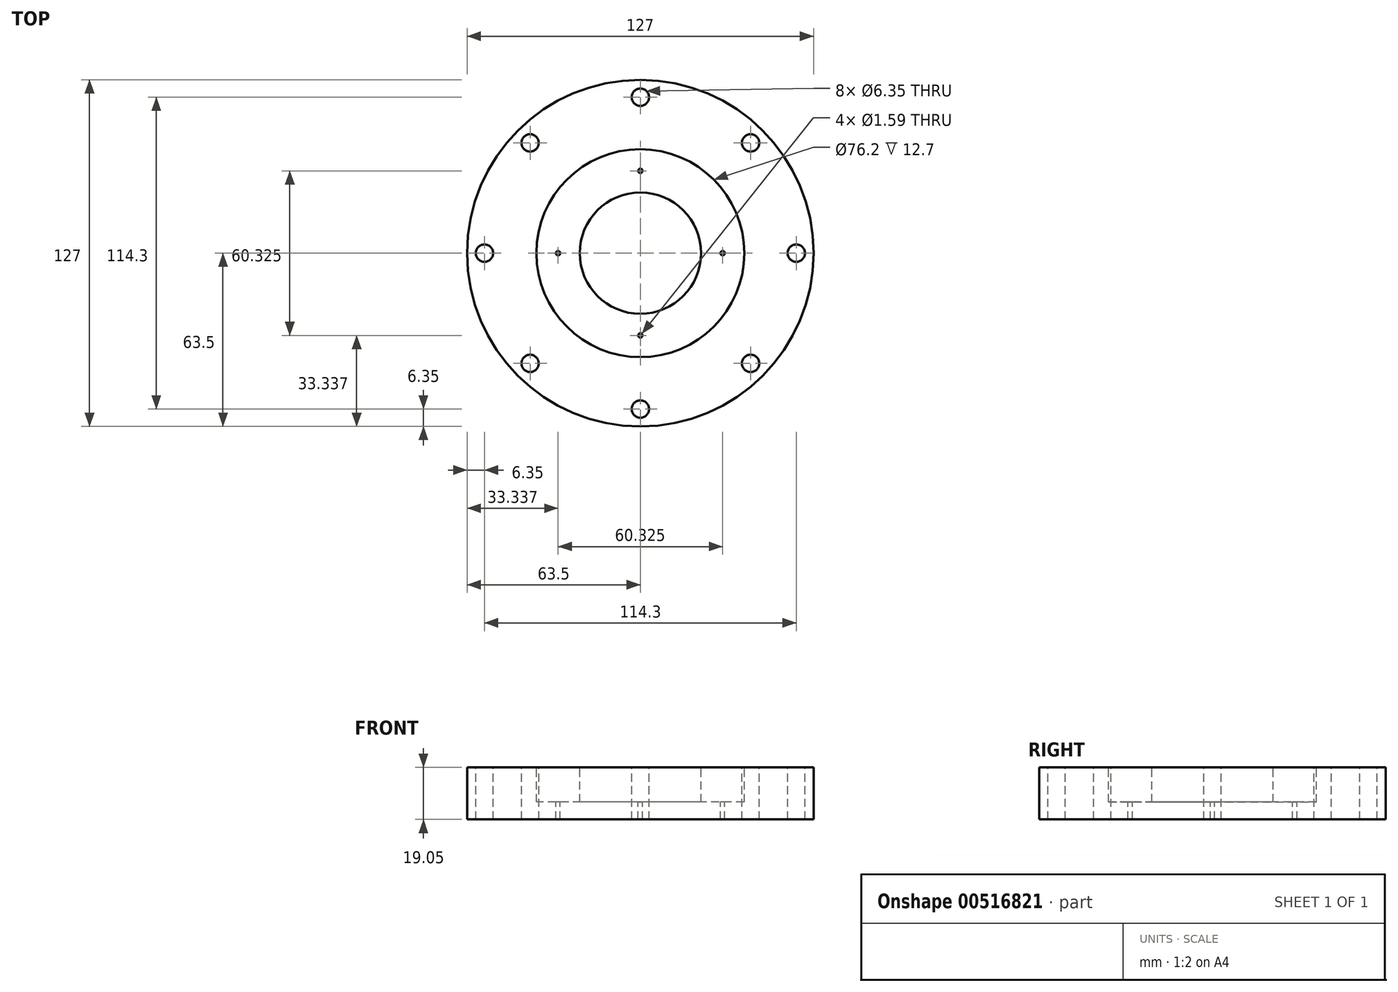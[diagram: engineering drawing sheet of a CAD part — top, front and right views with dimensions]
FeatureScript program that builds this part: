
annotation { "Feature Type Name" : "Feature", "Feature Type Description" : "" }
export const myFeature = defineFeature(function(context is Context, id is Id, definition is map)
    precondition{}
    {
        {
            var Q0;
            Q0=qCreatedBy(makeId("Top.planeOp"),FACE);
            var sketch = newSketch(context, id + "F0", { "sketchPlane" : qUnion([Q0])});
            skCircle(sketch, "E0", {"center": v(0, 0) * mm, "radius": 63.5 * mm});
            skSolve(sketch);
        }
        {
            var Q0;
            Q0 = qSketchRegion(id + "F0", true);
            extrude(context, id + "F1", {"entities" : qUnion([Q0]), "depth" : 19.05 * mm, "offsetDistance" : 25.4 * mm});
        }
        {
            var Q0;
            Q0=makeQuery(id+"F1.opExtrude","CAP_FACE",FACE,{"disambiguationData":[OSD([sQuery(id+"F0.wireOp",EDGE,"E0")])],"isStart":false});
            var sketch = newSketch(context, id + "F2", { "sketchPlane" : qUnion([Q0])});
            skArc(sketch, "E1", {"start": v(0, 57.15) * mm, "mid": v(-20.4, 53.39) * mm, "end": v(-38.1, 42.6) * mm});
            skCircle(sketch, "E2", {"center": v(0, 0) * mm, "radius": 38.1 * mm});
            skCircle(sketch, "E3", {"center": v(0, 0) * mm, "radius": 22.23 * mm});
            skCircle(sketch, "E4", {"center": v(0, 57.15) * mm, "radius": 3.18 * mm});
            skCircle(sketch, "E5.1.0", {"center": v(-40.41, 40.41) * mm, "radius": 3.18 * mm});
            skCircle(sketch, "E5.2.0", {"center": v(-57.15, 0) * mm, "radius": 3.18 * mm});
            skCircle(sketch, "E5.3.0", {"center": v(-40.41, -40.41) * mm, "radius": 3.18 * mm});
            skCircle(sketch, "E5.4.0", {"center": v(0, -57.15) * mm, "radius": 3.18 * mm});
            skCircle(sketch, "E5.5.0", {"center": v(40.41, -40.41) * mm, "radius": 3.18 * mm});
            skCircle(sketch, "E5.6.0", {"center": v(57.15, 0) * mm, "radius": 3.18 * mm});
            skCircle(sketch, "E5.7.0", {"center": v(40.41, 40.41) * mm, "radius": 3.18 * mm});
            skArc(sketch, "E6.trimOffspring", {"start": v(40.41, 40.41) * mm, "mid": v(23.33, 52.17) * mm, "end": v(3.17, 57.06) * mm});
            skArc(sketch, "E7.trimOffspring", {"start": v(57.06, 3.17) * mm, "mid": v(52.8, 21.87) * mm, "end": v(42.6, 38.1) * mm});
            skArc(sketch, "E8.trimOffspring", {"start": v(42.6, -38.1) * mm, "mid": v(53.39, -20.4) * mm, "end": v(57.15, 0) * mm});
            skArc(sketch, "E9.trimOffspring", {"start": v(3.17, -57.06) * mm, "mid": v(23.33, -52.17) * mm, "end": v(40.41, -40.41) * mm});
            skArc(sketch, "E10.trimOffspring", {"start": v(-38.1, -42.6) * mm, "mid": v(-20.4, -53.39) * mm, "end": v(0, -57.15) * mm});
            skArc(sketch, "E11.trimOffspring", {"start": v(-57.06, -3.17) * mm, "mid": v(-52.17, -23.33) * mm, "end": v(-40.41, -40.41) * mm});
            skArc(sketch, "E12.trimOffspring", {"start": v(-40.41, 40.41) * mm, "mid": v(-52.8, 21.87) * mm, "end": v(-57.15, 0) * mm});
            skSolve(sketch);
        }
        {
            var Q0;
            Q0=makeQuery(id+"F2.imprint","IMPRINT",FACE,{"disambiguationData":[TD([[makeQuery(id+"F2.imprint","IMPRINT",EDGE,{"derivedFrom":sQuery(id+"F2.wireOp",EDGE,"E2")}),1.0]])]});
            extrude(context, id + "F3", {"entities" : qUnion([Q0]), "operationType" : NewBodyOperationType.REMOVE, "oppositeDirection" : true, "depth" : 12.7 * mm, "offsetDistance" : 25.4 * mm});
        }
        {
            var Q0;
            {var subQ0=sQuery(id+"F0.wireOp",EDGE,"E0");Q0=makeQuery(id+"F3.boolean.opBoolean","SPLIT",FACE,{"disambiguationData":[TD([makeQuery(id+"F1.opExtrude","SWEPT_FACE",FACE,{"disambiguationData":[OSD([subQ0])]})])],"derivedFrom":makeQuery(id+"F1.opExtrude","CAP_FACE",FACE,{"disambiguationData":[OSD([subQ0])],"isStart":false})});}
            var sketch = newSketch(context, id + "F4", { "sketchPlane" : qUnion([Q0])});
            skArc(sketch, "E13", {"start": v(-40.41, 40.41) * mm, "mid": v(-52.17, 23.33) * mm, "end": v(-57.06, 3.17) * mm});
            skCircle(sketch, "E14", {"center": v(0, 57.15) * mm, "radius": 3.18 * mm});
            skCircle(sketch, "E15.1.0", {"center": v(-40.41, 40.41) * mm, "radius": 3.18 * mm});
            skCircle(sketch, "E15.2.0", {"center": v(-57.15, 0) * mm, "radius": 3.18 * mm});
            skCircle(sketch, "E15.3.0", {"center": v(-40.41, -40.41) * mm, "radius": 3.18 * mm});
            skCircle(sketch, "E15.4.0", {"center": v(0, -57.15) * mm, "radius": 3.18 * mm});
            skCircle(sketch, "E15.5.0", {"center": v(40.41, -40.41) * mm, "radius": 3.18 * mm});
            skCircle(sketch, "E15.6.0", {"center": v(57.15, 0) * mm, "radius": 3.18 * mm});
            skCircle(sketch, "E15.7.0", {"center": v(40.41, 40.41) * mm, "radius": 3.18 * mm});
            skArc(sketch, "E16.trimOffspring", {"start": v(0, 57.15) * mm, "mid": v(-20.4, 53.39) * mm, "end": v(-38.1, 42.6) * mm});
            skArc(sketch, "E17.trimOffspring", {"start": v(40.41, 40.41) * mm, "mid": v(23.33, 52.17) * mm, "end": v(3.17, 57.06) * mm});
            skArc(sketch, "E18.trimOffspring", {"start": v(57.15, 0) * mm, "mid": v(53.39, 20.4) * mm, "end": v(42.6, 38.1) * mm});
            skArc(sketch, "E19.trimOffspring", {"start": v(40.41, -40.41) * mm, "mid": v(52.17, -23.33) * mm, "end": v(57.06, -3.17) * mm});
            skArc(sketch, "E20.trimOffspring", {"start": v(0, -57.15) * mm, "mid": v(20.4, -53.39) * mm, "end": v(38.1, -42.6) * mm});
            skArc(sketch, "E21.trimOffspring", {"start": v(-40.41, -40.41) * mm, "mid": v(-23.33, -52.17) * mm, "end": v(-3.17, -57.06) * mm});
            skArc(sketch, "E22.trimOffspring", {"start": v(-57.15, 0) * mm, "mid": v(-53.39, -20.4) * mm, "end": v(-42.6, -38.1) * mm});
            skSolve(sketch);
        }
        {
            var Q0;
            {var subQ0=sQuery(id+"F4.wireOp",EDGE,"E15.2.0");var subQ1=makeQuery(id+"F4.imprint","INTERSECT",VERTEX,{"derivedFrom":[sQuery(id+"F4.wireOp",EDGE,"E13"),subQ0]});Q0=makeQuery(id+"F4.imprint","IMPRINT",FACE,{"disambiguationData":[TD([[makeQuery(id+"F4.imprint","IMPRINT",EDGE,{"disambiguationData":[TD([[subQ1,1.0]])],"derivedFrom":subQ0}),1.0]])]});}
            var Q1;
            {var subQ0=sQuery(id+"F4.wireOp",EDGE,"E15.1.0");var subQ1=makeQuery(id+"F4.imprint","INTERSECT",VERTEX,{"derivedFrom":[subQ0,sQuery(id+"F4.wireOp",EDGE,"E16.trimOffspring")]});Q1=makeQuery(id+"F4.imprint","IMPRINT",FACE,{"disambiguationData":[TD([[makeQuery(id+"F4.imprint","IMPRINT",EDGE,{"disambiguationData":[TD([[subQ1,1.0]])],"derivedFrom":subQ0}),1.0]])]});}
            var Q2;
            {var subQ0=sQuery(id+"F4.wireOp",EDGE,"E14");var subQ1=makeQuery(id+"F4.imprint","INTERSECT",VERTEX,{"derivedFrom":[subQ0,sQuery(id+"F4.wireOp",EDGE,"E17.trimOffspring")]});Q2=makeQuery(id+"F4.imprint","IMPRINT",FACE,{"disambiguationData":[TD([[makeQuery(id+"F4.imprint","IMPRINT",EDGE,{"disambiguationData":[TD([[subQ1,1.0]])],"derivedFrom":subQ0}),1.0]])]});}
            var Q3;
            {var subQ0=sQuery(id+"F4.wireOp",EDGE,"E15.7.0");var subQ1=makeQuery(id+"F4.imprint","INTERSECT",VERTEX,{"derivedFrom":[subQ0,sQuery(id+"F4.wireOp",EDGE,"E18.trimOffspring")]});Q3=makeQuery(id+"F4.imprint","IMPRINT",FACE,{"disambiguationData":[TD([[makeQuery(id+"F4.imprint","IMPRINT",EDGE,{"disambiguationData":[TD([[subQ1,1.0]])],"derivedFrom":subQ0}),1.0]])]});}
            var Q4;
            {var subQ0=sQuery(id+"F4.wireOp",EDGE,"E15.6.0");var subQ1=makeQuery(id+"F4.imprint","INTERSECT",VERTEX,{"derivedFrom":[subQ0,sQuery(id+"F4.wireOp",EDGE,"E19.trimOffspring")]});Q4=makeQuery(id+"F4.imprint","IMPRINT",FACE,{"disambiguationData":[TD([[makeQuery(id+"F4.imprint","IMPRINT",EDGE,{"disambiguationData":[TD([[subQ1,1.0]])],"derivedFrom":subQ0}),1.0]])]});}
            var Q5;
            {var subQ0=sQuery(id+"F4.wireOp",EDGE,"E15.5.0");var subQ1=makeQuery(id+"F4.imprint","INTERSECT",VERTEX,{"derivedFrom":[subQ0,sQuery(id+"F4.wireOp",EDGE,"E20.trimOffspring")]});Q5=makeQuery(id+"F4.imprint","IMPRINT",FACE,{"disambiguationData":[TD([[makeQuery(id+"F4.imprint","IMPRINT",EDGE,{"disambiguationData":[TD([[subQ1,1.0]])],"derivedFrom":subQ0}),1.0]])]});}
            var Q6;
            {var subQ0=sQuery(id+"F4.wireOp",EDGE,"E15.4.0");var subQ1=makeQuery(id+"F4.imprint","INTERSECT",VERTEX,{"derivedFrom":[subQ0,sQuery(id+"F4.wireOp",EDGE,"E21.trimOffspring")]});Q6=makeQuery(id+"F4.imprint","IMPRINT",FACE,{"disambiguationData":[TD([[makeQuery(id+"F4.imprint","IMPRINT",EDGE,{"disambiguationData":[TD([[subQ1,1.0]])],"derivedFrom":subQ0}),1.0]])]});}
            var Q7;
            {var subQ0=sQuery(id+"F4.wireOp",EDGE,"E15.3.0");var subQ1=makeQuery(id+"F4.imprint","INTERSECT",VERTEX,{"derivedFrom":[subQ0,sQuery(id+"F4.wireOp",EDGE,"E22.trimOffspring")]});Q7=makeQuery(id+"F4.imprint","IMPRINT",FACE,{"disambiguationData":[TD([[makeQuery(id+"F4.imprint","IMPRINT",EDGE,{"disambiguationData":[TD([[subQ1,1.0]])],"derivedFrom":subQ0}),1.0]])]});}
            extrude(context, id + "F5", {"entities" : qUnion([Q0, Q1, Q2, Q3, Q4, Q5, Q6, Q7]), "operationType" : NewBodyOperationType.REMOVE, "oppositeDirection" : true, "depth" : 25.4 * mm, "offsetDistance" : 25.4 * mm});
        }
        {
            var Q0;
            Q0=makeQuery(id+"F3.boolean.opBoolean","COPY",FACE,{"derivedFrom":makeQuery(id+"F3.opExtrude","CAP_FACE",FACE,{"disambiguationData":[OSD([sQuery(id+"F2.wireOp",EDGE,"E2"),sQuery(id+"F2.wireOp",EDGE,"E3")])],"isStart":false})});
            var sketch = newSketch(context, id + "F6", { "sketchPlane" : qUnion([Q0])});
            skArc(sketch, "E23", {"start": v(0, 30.16) * mm, "mid": v(-21.33, 21.33) * mm, "end": v(-30.16, 0) * mm});
            skCircle(sketch, "E24", {"center": v(0, 30.16) * mm, "radius": 0.8 * mm});
            skCircle(sketch, "E25.1.0", {"center": v(30.16, 0) * mm, "radius": 0.8 * mm});
            skCircle(sketch, "E25.2.0", {"center": v(0, -30.16) * mm, "radius": 0.8 * mm});
            skCircle(sketch, "E25.3.0", {"center": v(-30.16, 0) * mm, "radius": 0.8 * mm});
            skLineSegment(sketch, "E25.anchor1", {"start": v(0, 0) * mm, "end": v(0, 30.16) * mm, "construction": true});
            skLineSegment(sketch, "E25.anchor2", {"start": v(0, 0) * mm, "end": v(-30.16, 0) * mm, "construction": true});
            skArc(sketch, "E26.trimOffspring", {"start": v(30.16, 0) * mm, "mid": v(21.6, 21.05) * mm, "end": v(0.8, 30.15) * mm});
            skArc(sketch, "E27.trimOffspring", {"start": v(0, -30.16) * mm, "mid": v(21.05, -21.6) * mm, "end": v(30.15, -0.8) * mm});
            skArc(sketch, "E28.trimOffspring", {"start": v(-30.15, -0.8) * mm, "mid": v(-21.33, -21.33) * mm, "end": v(-0.8, -30.15) * mm});
            skSolve(sketch);
        }
        {
            var Q0;
            {var subQ0=sQuery(id+"F6.wireOp",EDGE,"E25.3.0");var subQ1=makeQuery(id+"F6.imprint","INTERSECT",VERTEX,{"derivedFrom":[subQ0,sQuery(id+"F6.wireOp",EDGE,"E28.trimOffspring")]});Q0=makeQuery(id+"F6.imprint","IMPRINT",FACE,{"disambiguationData":[TD([[makeQuery(id+"F6.imprint","IMPRINT",EDGE,{"disambiguationData":[TD([[subQ1,-1.0]])],"derivedFrom":subQ0}),1.0]])]});}
            var Q1;
            {var subQ0=sQuery(id+"F6.wireOp",EDGE,"E25.2.0");var subQ1=makeQuery(id+"F6.imprint","INTERSECT",VERTEX,{"derivedFrom":[subQ0,sQuery(id+"F6.wireOp",EDGE,"E28.trimOffspring")]});Q1=makeQuery(id+"F6.imprint","IMPRINT",FACE,{"disambiguationData":[TD([[makeQuery(id+"F6.imprint","IMPRINT",EDGE,{"disambiguationData":[TD([[subQ1,1.0]])],"derivedFrom":subQ0}),1.0]])]});}
            var Q2;
            {var subQ0=sQuery(id+"F6.wireOp",EDGE,"E25.1.0");var subQ1=makeQuery(id+"F6.imprint","INTERSECT",VERTEX,{"derivedFrom":[subQ0,sQuery(id+"F6.wireOp",EDGE,"E27.trimOffspring")]});Q2=makeQuery(id+"F6.imprint","IMPRINT",FACE,{"disambiguationData":[TD([[makeQuery(id+"F6.imprint","IMPRINT",EDGE,{"disambiguationData":[TD([[subQ1,1.0]])],"derivedFrom":subQ0}),1.0]])]});}
            var Q3;
            {var subQ0=sQuery(id+"F6.wireOp",EDGE,"E24");var subQ1=makeQuery(id+"F6.imprint","INTERSECT",VERTEX,{"derivedFrom":[subQ0,sQuery(id+"F6.wireOp",EDGE,"E26.trimOffspring")]});Q3=makeQuery(id+"F6.imprint","IMPRINT",FACE,{"disambiguationData":[TD([[makeQuery(id+"F6.imprint","IMPRINT",EDGE,{"disambiguationData":[TD([[subQ1,1.0]])],"derivedFrom":subQ0}),1.0]])]});}
            extrude(context, id + "F7", {"entities" : qUnion([Q0, Q1, Q2, Q3]), "operationType" : NewBodyOperationType.REMOVE, "oppositeDirection" : true, "depth" : 25.4 * mm, "offsetDistance" : 25.4 * mm});
        }
    });
